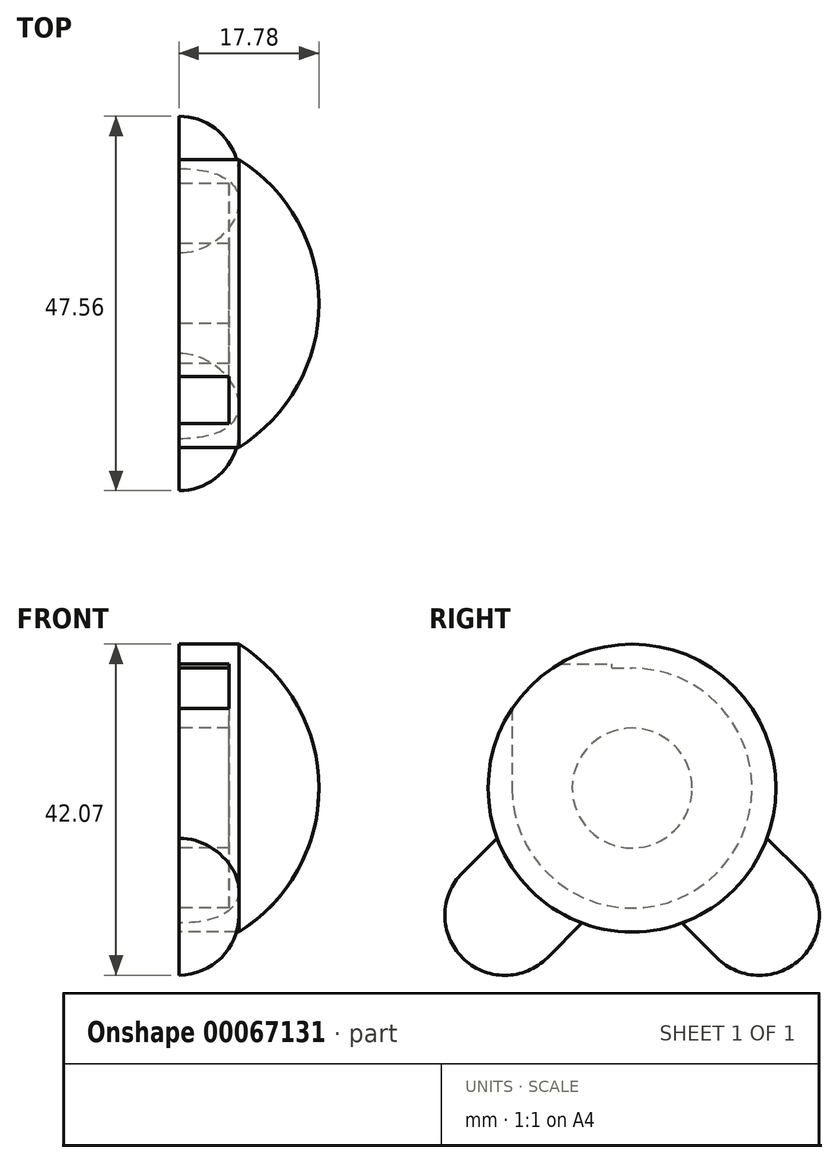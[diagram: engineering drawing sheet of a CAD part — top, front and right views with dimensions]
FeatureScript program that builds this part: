
annotation { "Feature Type Name" : "Feature", "Feature Type Description" : "" }
export const myFeature = defineFeature(function(context is Context, id is Id, definition is map)
    precondition{}
    {
        {
            var Q0;
            Q0=qCreatedBy(makeId("Right.planeOp"),FACE);
            var sketch = newSketch(context, id + "F0", { "sketchPlane" : qUnion([Q0])});
            skLineSegment(sketch, "E0", {"start": v(-25.4, 15.24) * mm, "end": v(0, 15.24) * mm});
            skArc(sketch, "E1", {"start": v(-15.24, 0) * mm, "mid": v(10.78, -10.78) * mm, "end": v(0, 15.24) * mm});
            skLineSegment(sketch, "E2", {"start": v(-25.4, 15.24) * mm, "end": v(-25.4, 10.16) * mm});
            skLineSegment(sketch, "E3", {"start": v(-25.4, 10.16) * mm, "end": v(-15.24, 10.16) * mm});
            skLineSegment(sketch, "E4", {"start": v(-15.24, 10.16) * mm, "end": v(-15.24, 0) * mm});
            skLineSegment(sketch, "E5.top", {"start": v(-15.24, 15.75) * mm, "end": v(-2.54, 15.75) * mm});
            skLineSegment(sketch, "E5.left", {"start": v(-15.24, 15.24) * mm, "end": v(-15.24, 15.75) * mm});
            skLineSegment(sketch, "E5.right", {"start": v(-2.54, 15.24) * mm, "end": v(-2.54, 15.75) * mm});
            skCircle(sketch, "E6", {"center": v(0, 0) * mm, "radius": 7.62 * mm});
            skSolve(sketch);
        }
        {
            var Q0;
            Q0=qCreatedBy(makeId("Front.planeOp"),FACE);
            var sketch = newSketch(context, id + "F1", { "sketchPlane" : qUnion([Q0])});
            skLineSegment(sketch, "E7.bottom", {"start": v(0, 18.29) * mm, "end": v(7.62, 18.29) * mm});
            skLineSegment(sketch, "E7.top", {"start": v(0, 0) * mm, "end": v(7.62, 0) * mm});
            skLineSegment(sketch, "E7.left", {"start": v(0, 18.29) * mm, "end": v(0, 0) * mm});
            skLineSegment(sketch, "E7.right", {"start": v(7.62, 18.29) * mm, "end": v(7.62, 0) * mm});
            skArc(sketch, "E8", {"start": v(17.78, 0) * mm, "mid": v(15.07, 10.46) * mm, "end": v(7.62, 18.29) * mm});
            skLineSegment(sketch, "E9", {"start": v(17.78, 0) * mm, "end": v(7.62, 0) * mm});
            skSolve(sketch);
        }
        {
            var Q0;
            Q0 = qSketchRegion(id + "F1", true);
            var Q1;
            Q1=sQuery(id+"F1.wireOp",EDGE,"E7.top");
            revolve(context, id + "F2", {"entities" : qUnion([Q0]), "axis" : qUnion([Q1]), "revolveType" : RevolveType.FULL});
        }
        {
            var Q0;
            Q0=qCreatedBy(makeId("Right.planeOp"),FACE);
            var sketch = newSketch(context, id + "F3", { "sketchPlane" : qUnion([Q0])});
            skLineSegment(sketch, "E10", {"start": v(0, 0) * mm, "end": v(-16.16, -16.16) * mm});
            skLineSegment(sketch, "E11.MirrorCS", {"start": v(0, 0) * mm, "end": v(16.16, -16.16) * mm});
            skLineSegment(sketch, "E12", {"start": v(-12.57, -1.8) * mm, "end": v(-21.55, -10.78) * mm});
            skLineSegment(sketch, "E13", {"start": v(-21.55, -10.78) * mm, "end": v(-16.16, -16.16) * mm});
            skArc(sketch, "E14", {"start": v(-21.55, -10.78) * mm, "mid": v(-23.78, -16.16) * mm, "end": v(-21.55, -21.55) * mm});
            skLineSegment(sketch, "E15", {"start": v(-16.16, -16.16) * mm, "end": v(-21.55, -21.55) * mm});
            skLineSegment(sketch, "E16", {"start": v(-12.57, -1.8) * mm, "end": v(-7.18, -7.18) * mm});
            skLineSegment(sketch, "E17.MirrorCS", {"start": v(12.57, -1.8) * mm, "end": v(7.18, -7.18) * mm});
            skLineSegment(sketch, "E18.MirrorCS", {"start": v(12.57, -1.8) * mm, "end": v(21.55, -10.78) * mm});
            skLineSegment(sketch, "E19.MirrorCS", {"start": v(21.55, -10.78) * mm, "end": v(16.16, -16.16) * mm});
            skLineSegment(sketch, "E20.MirrorCS", {"start": v(16.16, -16.16) * mm, "end": v(21.55, -21.55) * mm});
            skArc(sketch, "E21.MirrorCS", {"start": v(21.55, -10.78) * mm, "mid": v(23.78, -16.16) * mm, "end": v(21.55, -21.55) * mm});
            skSolve(sketch);
        }
        {
            var Q0;
            Q0=makeQuery(id+"F3.imprint","IMPRINT",FACE,{"disambiguationData":[TD([[makeQuery(id+"F3.imprint","IMPRINT",EDGE,{"derivedFrom":sQuery(id+"F3.wireOp",EDGE,"E12")}),1.0]])]});
            var Q1;
            Q1=makeQuery(id+"F3.imprint","IMPRINT",FACE,{"disambiguationData":[TD([[makeQuery(id+"F3.imprint","IMPRINT",EDGE,{"derivedFrom":sQuery(id+"F3.wireOp",EDGE,"E13")}),-1.0]])]});
            var Q2;
            Q2=sQuery(id+"F3.wireOp",EDGE,"E10");
            revolve(context, id + "F4", {"operationType" : NewBodyOperationType.ADD, "entities" : qUnion([Q0, Q1]), "axis" : qUnion([Q2]), "revolveType" : RevolveType.ONE_DIRECTION, "oppositeDirection" : true, "angle" : 180 * degree});
        }
        {
            var Q0;
            {var subQ2=sQuery(id+"F3.wireOp",EDGE,"E17.MirrorCS");Q0=makeQuery(id+"F3.imprint","IMPRINT",FACE,{"disambiguationData":[TD([[makeQuery(id+"F3.imprint","IMPRINT",EDGE,{"derivedFrom":subQ2}),1.0]])]});}
            var Q1;
            Q1=makeQuery(id+"F3.imprint","IMPRINT",FACE,{"disambiguationData":[TD([[makeQuery(id+"F3.imprint","IMPRINT",EDGE,{"derivedFrom":sQuery(id+"F3.wireOp",EDGE,"E19.MirrorCS")}),1.0]])]});
            var Q2;
            Q2=sQuery(id+"F3.wireOp",EDGE,"E11.MirrorCS");
            revolve(context, id + "F5", {"operationType" : NewBodyOperationType.ADD, "entities" : qUnion([Q0, Q1]), "axis" : qUnion([Q2]), "revolveType" : RevolveType.ONE_DIRECTION, "angle" : 180 * degree});
        }
        {
            var Q0;
            Q0 = qSketchRegion(id + "F0", true);
            extrude(context, id + "F6", {"entities" : qUnion([Q0]), "operationType" : NewBodyOperationType.REMOVE, "depth" : 6.35 * mm});
        }
    });
